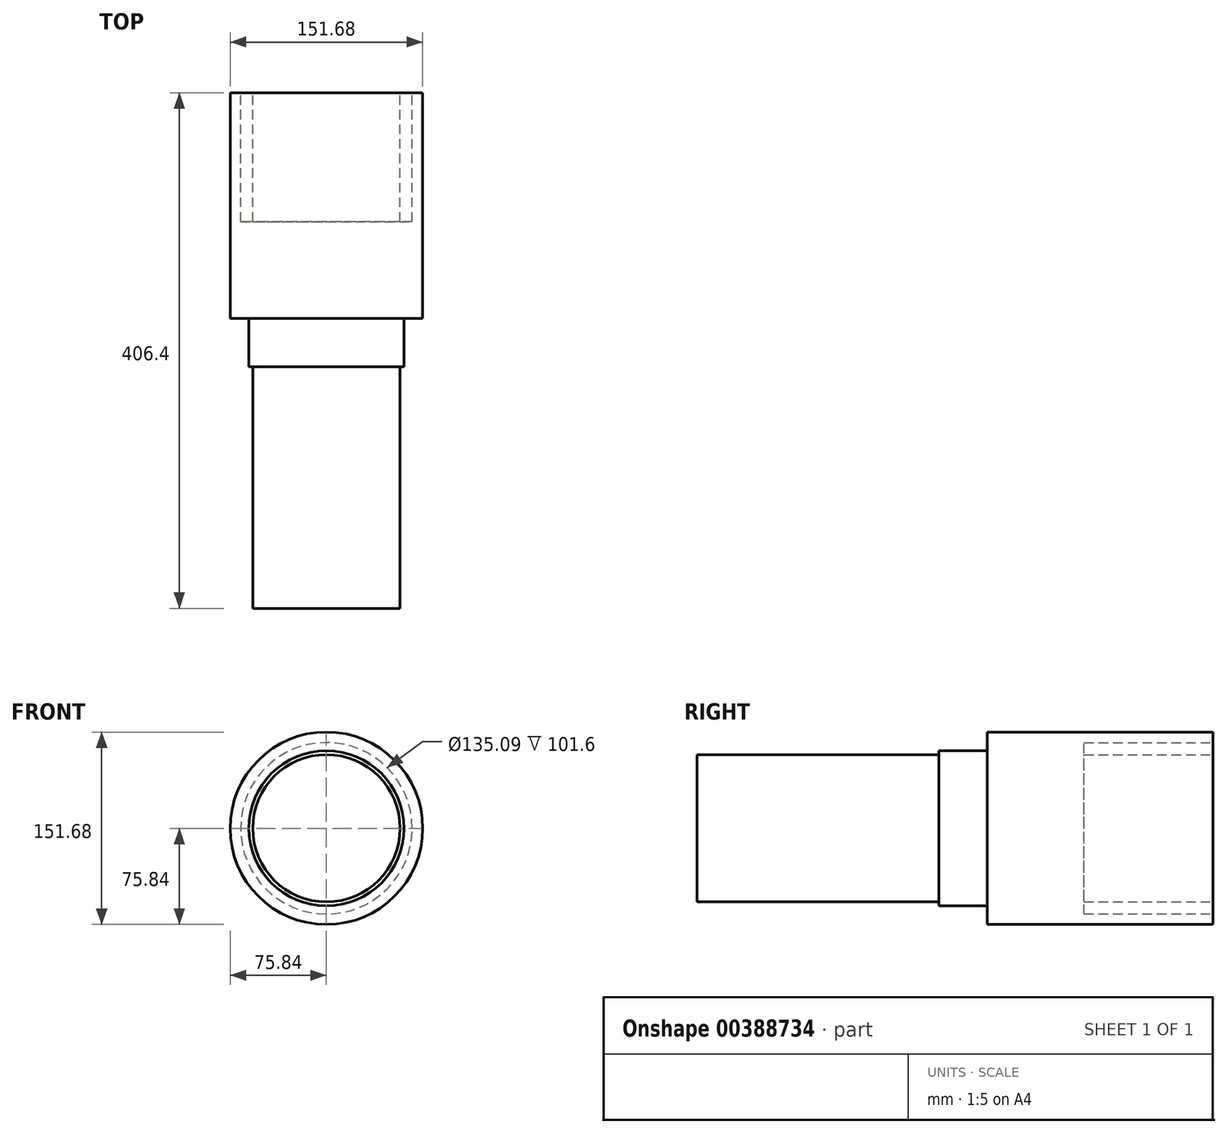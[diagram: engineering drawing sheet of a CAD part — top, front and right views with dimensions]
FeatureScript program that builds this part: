
annotation { "Feature Type Name" : "Feature", "Feature Type Description" : "" }
export const myFeature = defineFeature(function(context is Context, id is Id, definition is map)
    precondition{}
    {
        {
            var Q0;
            Q0=qCreatedBy(makeId("Front.planeOp"),FACE);
            var sketch = newSketch(context, id + "F0", { "sketchPlane" : qUnion([Q0])});
            skCircle(sketch, "E0", {"center": v(0, 0) * mm, "radius": 75.84 * mm});
            skSolve(sketch);
        }
        {
            var Q0;
            Q0=makeQuery(id+"F0.imprint","IMPRINT",FACE,{"disambiguationData":[TD([[makeQuery(id+"F0.imprint","IMPRINT",EDGE,{"derivedFrom":sQuery(id+"F0.wireOp",EDGE,"E0")}),1.0]])]});
            extrude(context, id + "F1", {"entities" : qUnion([Q0]), "depth" : 177.8 * mm});
        }
        {
            var Q0;
            Q0=qCreatedBy(makeId("Front.planeOp"),FACE);
            var sketch = newSketch(context, id + "F2", { "sketchPlane" : qUnion([Q0])});
            skCircle(sketch, "E1", {"center": v(0, 0) * mm, "radius": 61.13 * mm});
            skSolve(sketch);
        }
        {
            var Q0;
            Q0=qCreatedBy(makeId("Front.planeOp"),FACE);
            var sketch = newSketch(context, id + "F3", { "sketchPlane" : qUnion([Q0])});
            skCircle(sketch, "E2", {"center": v(0, 0) * mm, "radius": 17.42 * mm});
            skSolve(sketch);
        }
        {
            var Q0;
            Q0 = qSketchRegion(id + "F2", true);
            extrude(context, id + "F4", {"entities" : qUnion([Q0]), "operationType" : NewBodyOperationType.ADD, "depth" : 215.9 * mm});
        }
        {
            var Q0;
            Q0 = qSketchRegion(id + "F3", true);
            extrude(context, id + "F5", {"entities" : qUnion([Q0]), "operationType" : NewBodyOperationType.REMOVE, "depth" : 215.9 * mm});
        }
        {
            var Q0;
            Q0=qCreatedBy(makeId("Front.planeOp"),FACE);
            var sketch = newSketch(context, id + "F6", { "sketchPlane" : qUnion([Q0])});
            skCircle(sketch, "E3", {"center": v(0, 0) * mm, "radius": 67.55 * mm});
            skSolve(sketch);
        }
        {
            var Q0;
            Q0 = qSketchRegion(id + "F6", true);
            extrude(context, id + "F7", {"entities" : qUnion([Q0]), "operationType" : NewBodyOperationType.REMOVE, "depth" : 101.6 * mm});
        }
        {
            var Q0;
            Q0=qCreatedBy(makeId("Front.planeOp"),FACE);
            var sketch = newSketch(context, id + "F8", { "sketchPlane" : qUnion([Q0])});
            skCircle(sketch, "E4", {"center": v(0, 0) * mm, "radius": 58.02 * mm});
            skSolve(sketch);
        }
        {
            var Q0;
            Q0 = qSketchRegion(id + "F8", true);
            extrude(context, id + "F9", {"entities" : qUnion([Q0]), "operationType" : NewBodyOperationType.ADD, "depth" : 406.4 * mm});
        }
    });
